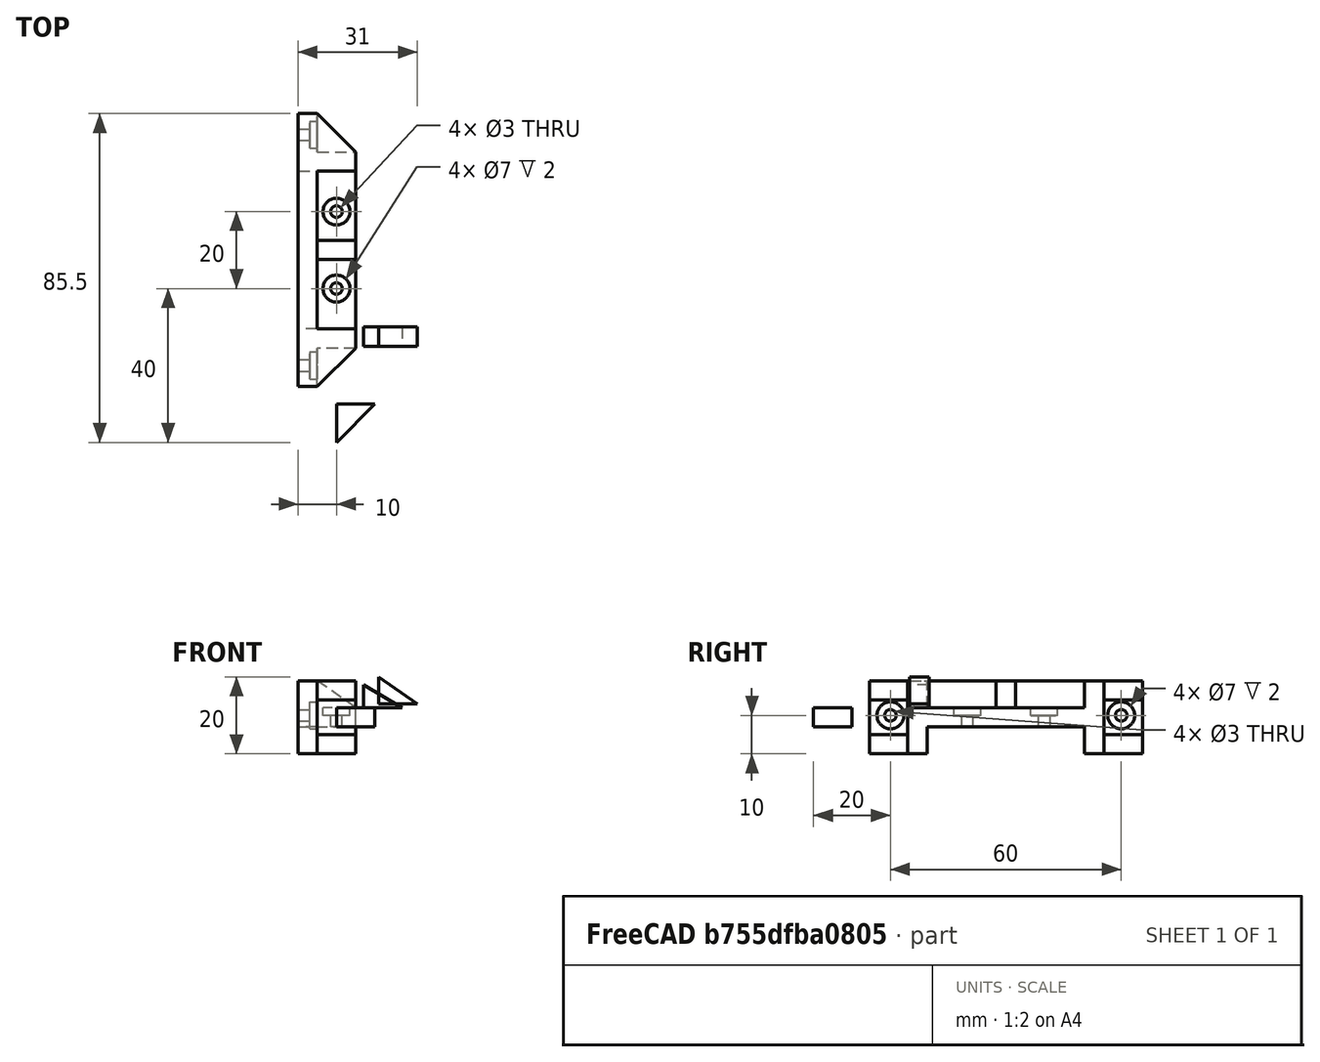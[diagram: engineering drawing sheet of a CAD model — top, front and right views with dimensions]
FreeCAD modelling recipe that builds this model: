
FCSTD DOCUMENT  (FreeCAD 0.18R14555 (Git shallow))
Label: y-mounter
License: All rights reserved
LicenseURL: http://en.wikipedia.org/wiki/All_rights_reserved
objects: Part::Box×8, Part::Cylinder×8, Part::Feature×7, Sketcher::SketchObject×3, PartDesign::Pad×3, PartDesign::Body×3, Part::MultiFuse×2, Part::Cut×1
note: 38 computed .brp shape members not serialized (recipe doc carries the construction recipe); baked Part::Feature solids carry a one-line shape summary decoded from their .brp

FEATURE [Part::Box] Box  label="Cube"
  AttacherType = Attacher::AttachEngine3D
  Height = 5
  Length = 15
  Width = 40
FEATURE [Part::Box] Box001  label="Cube001"
  AttacherType = Attacher::AttachEngine3D
  Height = 12
  Length = 5
  Placement = pos=(0,-15,0) rot=(0,0,1;0rad)
  Width = 70
FEATURE [Part::Cylinder] Cylinder
  Angle = 360
  AttacherType = Attacher::AttachEngine3D
  Height = 5
  Placement = pos=(10,10,0) rot=(0,0,1;0rad)
  Radius = 1.5
FEATURE [Part::Cylinder] Cylinder001
  Angle = 360
  AttacherType = Attacher::AttachEngine3D
  Height = 5
  Placement = pos=(10,30,0) rot=(0,0,1;0rad)
  Radius = 1.5
FEATURE [Part::Cylinder] Cylinder002
  Angle = 360
  AttacherType = Attacher::AttachEngine3D
  Height = 5
  Placement = pos=(-1e-15,-10,3) rot=(0,1,0;1.5708rad)
  Radius = 1.5
FEATURE [Part::Cylinder] Cylinder003
  Angle = 360
  AttacherType = Attacher::AttachEngine3D
  Height = 5
  Placement = pos=(-1e-15,50,3) rot=(0,1,0;1.5708rad)
  Radius = 1.5
FEATURE [Part::Cylinder] Cylinder004
  Angle = 360
  AttacherType = Attacher::AttachEngine3D
  Height = 2
  Placement = pos=(3,50,3) rot=(0,1,0;1.5708rad)
  Radius = 3.5
FEATURE [Part::Cylinder] Cylinder005
  Angle = 360
  AttacherType = Attacher::AttachEngine3D
  Height = 2
  Placement = pos=(3,-10,3) rot=(0,1,0;1.5708rad)
  Radius = 3.5
FEATURE [Part::Cylinder] Cylinder006
  Angle = 360
  AttacherType = Attacher::AttachEngine3D
  Height = 2
  Placement = pos=(10,30,3) rot=(0,0,1;0rad)
  Radius = 3.5
FEATURE [Part::Cylinder] Cylinder007
  Angle = 360
  AttacherType = Attacher::AttachEngine3D
  Height = 2
  Placement = pos=(10,10,3) rot=(0,0,1;0rad)
  Radius = 3.5
FEATURE [Part::Box] Box002  label="Cube002"
  AttacherType = Attacher::AttachEngine3D
  Height = 19
  Length = 5
  Placement = pos=(0,-15.5,-7) rot=(0,0,1;0rad)
  Width = 15
FEATURE [Part::Box] Box003  label="Cube003"
  AttacherType = Attacher::AttachEngine3D
  Height = 19
  Length = 5
  Placement = pos=(0,40.5,-7) rot=(0,0,1;0rad)
  Width = 15
FEATURE [Part::Box] Box004  label="Cube004"
  AttacherType = Attacher::AttachEngine3D
  Height = 5
  Length = 10
  Placement = pos=(5,-0.5,0) rot=(0,0,1;0rad)
  Width = 0.5
FEATURE [Part::Box] Box005  label="Cube005"
  AttacherType = Attacher::AttachEngine3D
  Height = 5
  Length = 10
  Placement = pos=(5,40,0) rot=(0,0,1;0rad)
  Width = 0.5
FEATURE [Part::Box] Box006  label="Cube006"
  AttacherType = Attacher::AttachEngine3D
  Height = 19
  Length = 10
  Placement = pos=(5,-5.5,-7) rot=(0,0,1;0rad)
  Width = 5
FEATURE [Part::Box] Box007  label="Cube007"
  AttacherType = Attacher::AttachEngine3D
  Height = 19
  Length = 10
  Placement = pos=(5,40.5,-7) rot=(0,0,1;0rad)
  Width = 5
FEATURE [Sketcher::SketchObject] Sketch
  MapMode = 5
  Support = -> [XY_Plane]
  sketch-geometry (3):
    g0: LineSegment StartX=10 StartY=-20 StartZ=0 EndX=10 EndY=-30 EndZ=0
    g1: LineSegment StartX=10 StartY=-30 StartZ=0 EndX=20 EndY=-20 EndZ=0
    g2: LineSegment StartX=20 StartY=-20 StartZ=0 EndX=10 EndY=-20 EndZ=0
  constraints (3):
    c: Coincident(g0,g1)
    c: Coincident(g1,g2)
    c: Coincident(g2,g0)
FEATURE [PartDesign::Pad] Pad
  Length = 5
  Length2 = 100
  Profile = -> Sketch
  Type = 0
FEATURE [PartDesign::Body] Body
  Group = -> [Sketch,Pad]
  Origin = -> Origin
  Tip = -> Pad
FEATURE [Part::Feature] Body001
  Placement = pos=(-5,14.5,-7) rot=(0,0,1;0rad)
  shape: bbox 10 x 10 x 5 mm, 5 faces (baked)
FEATURE [Part::Feature] Body002
  Placement = pos=(-15,35.5,-7) rot=(0,0,1;1.5708rad)
  shape: bbox 10 x 10 x 5 mm, 5 faces (baked)
FEATURE [Sketcher::SketchObject] Sketch001
  MapMode = 5
  Placement = pos=(0,0,0) rot=(1,0,0;1.5708rad)
  Support = -> [XZ_Plane001]
  sketch-geometry (3):
    g0: LineSegment StartX=17 StartY=11 StartZ=0 EndX=17 EndY=5 EndZ=0
    g1: LineSegment StartX=17 StartY=5 StartZ=0 EndX=27 EndY=5 EndZ=0
    g2: LineSegment StartX=27 StartY=5 StartZ=0 EndX=17 EndY=11 EndZ=0
  constraints (3):
    c: Coincident(g0,g1)
    c: Coincident(g1,g2)
    c: Coincident(g2,g0)
FEATURE [PartDesign::Pad] Pad001
  Length = 5
  Length2 = 100
  Placement = pos=(0,0,0) rot=(1,0,0;1.5708rad)
  Profile = -> Sketch001
  Type = 0
FEATURE [PartDesign::Body] Body003
  Group = -> [Sketch001,Pad001]
  Origin = -> Origin001
  Tip = -> Pad001
FEATURE [Part::Feature] Body003003
  Placement = pos=(-5,14.5,7) rot=(0,0,1;0rad)
  shape: bbox 10 x 10 x 5 mm, 5 faces (baked)
FEATURE [Part::Feature] Body003004
  Placement = pos=(-15,35.5,7) rot=(0,0,1;1.5708rad)
  shape: bbox 10 x 10 x 5 mm, 5 faces (baked)
FEATURE [Sketcher::SketchObject] Sketch002
  MapMode = 5
  Placement = pos=(0,0,0) rot=(1,0,0;1.5708rad)
  Support = -> [XZ_Plane002]
  sketch-geometry (3):
    g0: LineSegment StartX=21 StartY=13 StartZ=0 EndX=21 EndY=6 EndZ=0
    g1: LineSegment StartX=21 StartY=6 StartZ=0 EndX=31 EndY=6 EndZ=0
    g2: LineSegment StartX=31 StartY=6 StartZ=0 EndX=21 EndY=13 EndZ=0
  constraints (3):
    c: Coincident(g0,g1)
    c: Coincident(g1,g2)
    c: Coincident(g2,g0)
FEATURE [PartDesign::Pad] Pad002
  Length = 5
  Length2 = 100
  Placement = pos=(0,0,0) rot=(1,0,0;1.5708rad)
  Profile = -> Sketch002
  Type = 0
FEATURE [PartDesign::Body] Body003005
  Group = -> [Sketch002,Pad002]
  Origin = -> Origin002
  Tip = -> Pad002
FEATURE [Part::Feature] Body003005001  label="Body003006"
  Placement = pos=(-16,22.505,-1) rot=(0,0,1;0rad)
  shape: bbox 10 x 5 x 7 mm, 5 faces (baked)
FEATURE [Part::MultiFuse] Fusion
  Shapes = -> [Cylinder005,Cylinder,Cylinder002,Cylinder001,Cylinder003,Cylinder004,Cylinder006,Cylinder007]
FEATURE [Part::MultiFuse] Fusion001
  Shapes = -> [Body003005001,Body003004,Body003003,Box006,Box007,Body002,Body001,Box001,Box004,Box005,Box003,Box002,Box]
FEATURE [Part::Cut] Cut
  Base = -> Fusion001
  Tool = -> Fusion
FEATURE [Part::Feature] Cut001
  shape: bbox 15 x 71 x 19 mm, 43 faces (baked)
FEATURE [Part::Feature] Cut001_solid  label="Cut001 (Solid)"
  shape: bbox 15 x 71 x 19 mm, 43 faces (baked)
